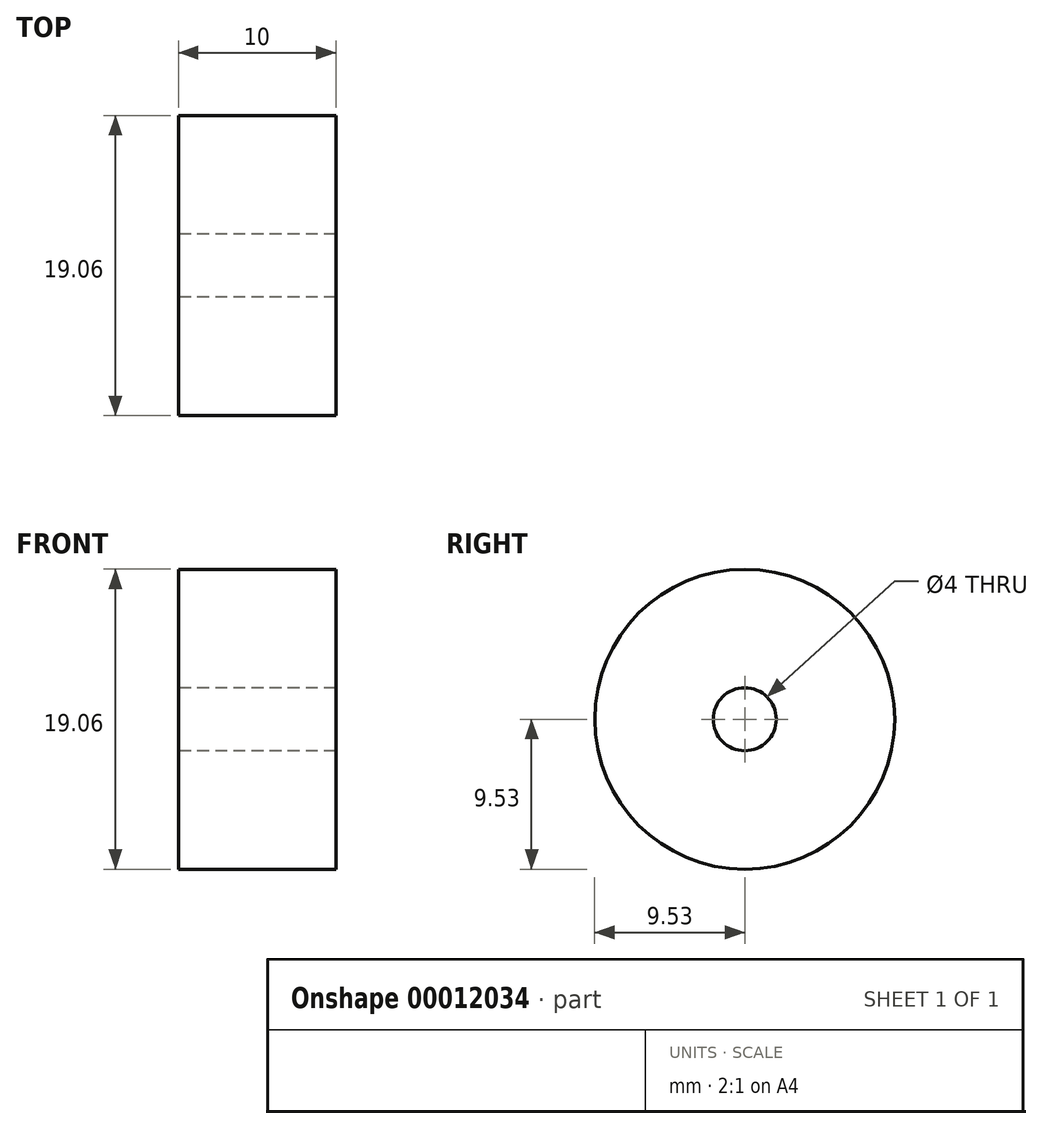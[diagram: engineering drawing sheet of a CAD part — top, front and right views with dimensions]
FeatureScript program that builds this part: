
annotation { "Feature Type Name" : "Feature", "Feature Type Description" : "" }
export const myFeature = defineFeature(function(context is Context, id is Id, definition is map)
    precondition{}
    {
        {
            var Q0;
            Q0=qCreatedBy(makeId("Right.planeOp"),FACE);
            var sketch = newSketch(context, id + "F0", { "sketchPlane" : qUnion([Q0])});
            skCircle(sketch, "E0", {"center": v(0, 0) * mm, "radius": 9.52 * mm});
            skCircle(sketch, "E1", {"center": v(0, 0) * mm, "radius": 2 * mm});
            skSolve(sketch);
        }
        {
            var Q0;
            Q0=makeQuery(id+"F0.imprint","IMPRINT",FACE,{"disambiguationData":[TD([[makeQuery(id+"F0.imprint","IMPRINT",EDGE,{"derivedFrom":sQuery(id+"F0.wireOp",EDGE,"E0")}),1.0]])]});
            extrude(context, id + "F1", {"entities" : qUnion([Q0]), "depth" : 10 * mm});
        }
    });
